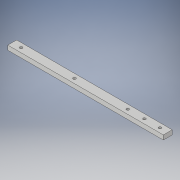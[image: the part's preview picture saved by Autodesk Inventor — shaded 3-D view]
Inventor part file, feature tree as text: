
AUTODESK INVENTOR PART (.ipt)
format: ipt  version: 2019 (Build 230136000, 136)  size: 98,816 bytes
history: native  units: in
note: dims shown in document units (in); Inventor stores cm internally (conversion verified against a paired STEP export)
features: extrude x1, sketch x1
ambient origin geometry x8: Origin, YZ Plane, XZ Plane, XY Plane, X Axis, Y Axis, Z Axis, Center Point
bodies: Solid1 (feature_tree)
feature tree (2):
  extrude  "Extrusion1"  [1 undecoded]
  sketch  "Sketch1"  dims[d7=0.1969in d8=0.0in]
note: 1 required parameter value undecoded (feature->parameter linkage not recoverable at this tier; creation-order binding heuristic only, values carry confidence <= 0.55)
